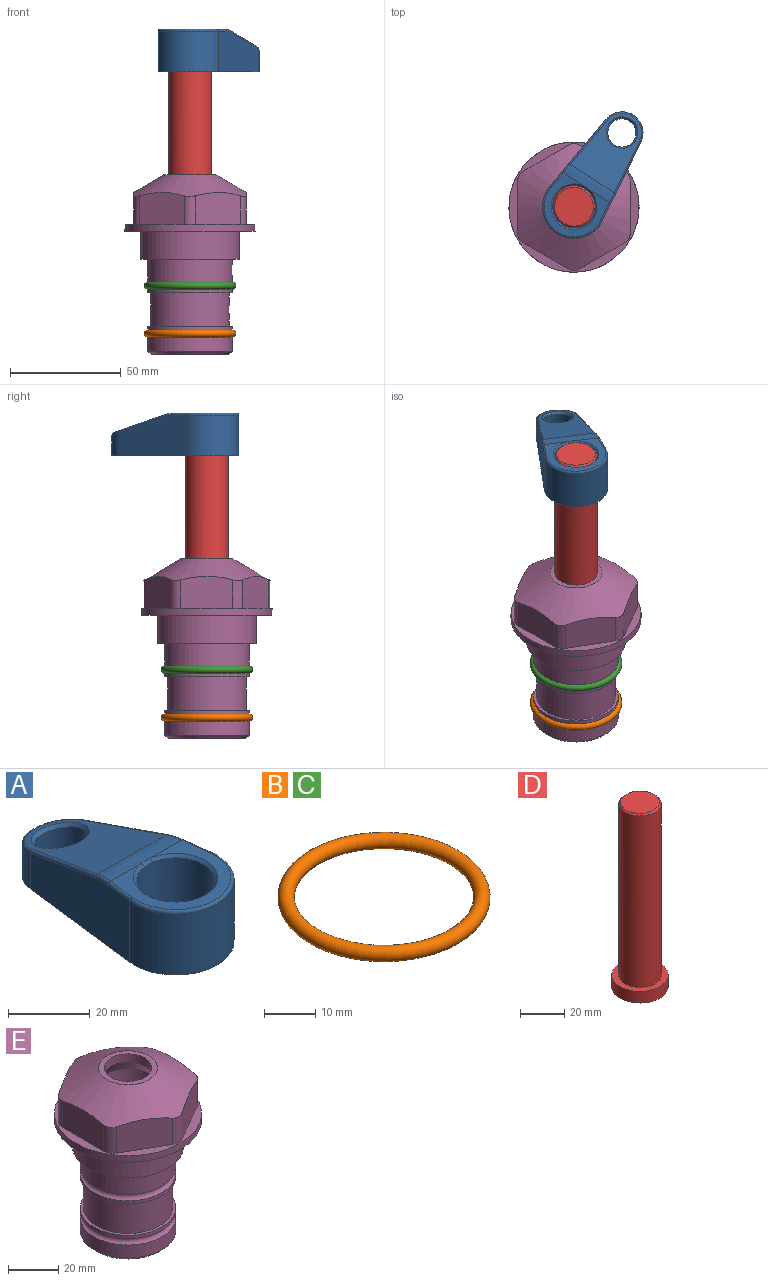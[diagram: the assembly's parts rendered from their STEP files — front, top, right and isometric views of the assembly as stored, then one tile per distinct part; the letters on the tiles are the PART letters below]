
ASSEMBLY  parts=5 mates=4
PART A: 31 faces, bbox 31.7x65.5x19.8 mm
  f0: plane 39.12x18.26mm, normal (0.99,0.12,0), area 612.2mm2, adj f1,f4,f7,f11,f13,f15
  f1: cylinder r=9.53mm len=18.91mm, axis (0,0,-1), area 296.1mm2, adj f0,f2,f7,f17
  f2: plane 39.12x18.26mm, normal (-0.99,0.12,0), area 612.2mm2, adj f1,f4,f7,f12,f14,f16
  f3: cylinder r=6.35mm len=12.7mm, axis (0,0,-1), area 362.4mm2, adj f7,f18
  f4: cylinder r=14.29mm len=28.58mm, axis (0,0,-1), area 882.2mm2, adj f0,f2,f7,f10
  f5: cylinder r=9.53mm len=19.05mm, axis (0,0,-1), area 1092.6mm2, adj f7,f19,f20
  f6: plane 26.99x23.69mm, normal (0,0,1), area 216.2mm2, adj f9,f10,f11,f12,f19
  f7: plane 63.5x28.58mm, normal (0,0,-1), area 661.8mm2, adj f0,f1,f2,f3,f4,f5,f22,f23
  f8: plane 33.52x23.6mm, normal (0,0.26,0.97), area 486mm2, adj f9,f15,f16,f17,f18
  f9: cylinder r=19.05mm len=24.72mm, axis (1,0,0), area 120.4mm2, adj f6,f8,f13,f14,f20
  f10: torus R=13.49mm, axis (0,0,1), area 59mm2, adj f4,f6,f11,f12
  f11: cylinder r=0.79mm len=8.67mm, axis (0.12,-0.99,0), area 10.8mm2, adj f0,f6,f10,f13
  f12: cylinder r=0.79mm len=8.67mm, axis (0.12,0.99,0), area 10.8mm2, adj f2,f6,f10,f14
  f13: bspline ~4.95x1.42mm, area 6.1mm2, adj f0,f9,f11,f15
  f14: bspline ~4.95x1.42mm, area 6.1mm2, adj f2,f9,f12,f16
  f15: cylinder r=0.79mm len=25.95mm, axis (0.12,-0.96,0.26), area 32.9mm2, adj f0,f8,f13,f17
  f16: cylinder r=0.79mm len=25.95mm, axis (0.12,0.96,-0.26), area 32.9mm2, adj f2,f8,f14,f17
  f17: bspline ~18.91x8.38mm, area 30mm2, adj f1,f8,f15,f16
  f18: bspline ~14.29x14.29mm, area 48.3mm2, adj f3,f8
  f19: cone r=9.53mm half-angle=45deg, axis (0,0,1), area 66.5mm2, adj f5,f6,f20
  f20: bspline ~3.22x0.96mm, area 3.5mm2, adj f5,f9,f19
  f21: plane 2.75x2.72mm, normal (0,0,-1), area 2.9mm2, adj f23,f25,f28
  f22: plane 23.05x15.88mm, normal (-0.99,-0.12,0), area 323.6mm2, adj f7,f25,f26,f27,f28,f29
  f23: plane 23.05x15.88mm, normal (0.99,-0.12,0), area 323.6mm2, adj f7,f21,f25,f27,f28,f30
  f24: cylinder r=9.53mm len=10.69mm, axis (0,0,-1), area 114.7mm2, adj f7,f27,f29,f30
  f25: cylinder r=12.7mm len=20.59mm, axis (0,0,-1), area 381.1mm2, adj f7,f21,f22,f23,f26,f28
  f26: plane 2.75x2.72mm, normal (0,0,-1), area 2.9mm2, adj f22,f25,f28
  f27: plane 19.72x18.37mm, normal (0,-0.26,-0.97), area 291.8mm2, adj f22,f23,f24,f28,f29,f30
  f28: cylinder r=15.88mm len=19.92mm, axis (1,0,0), area 54.8mm2, adj f21,f22,f23,f25,f26,f27
  f29: cylinder r=1.59mm len=11mm, axis (0,0,-1), area 34.7mm2, adj f7,f22,f24,f27
  f30: cylinder r=1.59mm len=11mm, axis (0,0,-1), area 34.7mm2, adj f7,f23,f24,f27
PART B: 1 faces, bbox 44.7x44.7x3.2 mm
  f0: torus R=19.05mm, axis (0,0,1), area 1193.9mm2
PART C: same geometry as B
PART D: 6 faces, bbox 25.4x25.4x101.6 mm
  f0: plane 17.46x17.46mm, normal (0,0,1), area 239.5mm2, adj f5
  f1: plane 25.4x25.4mm, normal (0,0,-1), area 506.7mm2, adj f2
  f2: cylinder r=12.7mm len=25.4mm, axis (0,0,1), area 506.7mm2, adj f1,f3
  f3: plane 25.4x25.4mm, normal (0,0,1), area 221.7mm2, adj f2,f4
  f4: cylinder r=9.53mm len=94.46mm, axis (0,0,1), area 5653mm2, adj f3,f5
  f5: cone r=8.73mm half-angle=45deg, axis (0,0,-1), area 64.4mm2, adj f0,f4
PART E: 36 faces, bbox 58.7x58.7x81 mm
  f0: cylinder r=17.78mm len=35.56mm, axis (0,0,1), area 1670.8mm2, adj f23,f24,f31
  f1: cylinder r=19.05mm len=38.1mm, axis (0,0,1), area 1191.9mm2, adj f26,f27,f30
  f2: plane 58.66x58.66mm, normal (0,0,-1), area 1150.6mm2, adj f3,f28
  f3: cylinder r=29.33mm len=58.66mm, axis (0,0,-1), area 585.1mm2, adj f2,f4
  f4: plane 58.66x58.66mm, normal (0,0,1), area 475.9mm2, adj f3,f5,f6,f7,f8,f9,f10,f11
  f5: plane 20.32x14.34mm, normal (-0.5,0.87,0), area 324.4mm2, adj f4,f15,f16,f17
  f6: plane 20.32x14.34mm, normal (0.5,0.87,0), area 324.4mm2, adj f4,f14,f15,f17
  f7: plane 23.48x14.34mm, normal (1,0,0), area 324.4mm2, adj f4,f13,f14,f17
  f8: plane 20.32x14.34mm, normal (0.5,-0.87,0), area 324.4mm2, adj f4,f12,f13,f17
  f9: plane 20.32x14.34mm, normal (-0.5,-0.87,0), area 324.4mm2, adj f4,f11,f12,f17
  f10: plane 23.48x14.34mm, normal (-1,0,0), area 324.4mm2, adj f4,f11,f16,f17
  f11: cylinder r=5.08mm len=12.85mm, axis (0,0,-1), area 67.2mm2, adj f4,f9,f10,f17
  f12: cylinder r=5.08mm len=12.85mm, axis (0,0,-1), area 67.2mm2, adj f4,f8,f9,f17
  f13: cylinder r=5.08mm len=12.85mm, axis (0,0,-1), area 67.2mm2, adj f4,f7,f8,f17
  f14: cylinder r=5.08mm len=12.85mm, axis (0,0,-1), area 67.2mm2, adj f4,f6,f7,f17
  f15: cylinder r=5.08mm len=12.85mm, axis (0,0,-1), area 67.2mm2, adj f4,f5,f6,f17
  f16: cylinder r=5.08mm len=12.85mm, axis (0,0,-1), area 67.2mm2, adj f4,f5,f10,f17
  f17: cone r=11.73mm half-angle=60deg, axis (0,0,-1), area 2071.8mm2, adj f5,f6,f7,f8,f9,f10,f11,f12
  f18: plane 23.46x23.46mm, normal (0,0,1), area 147.4mm2, adj f17,f35
  f19: plane 34.93x34.93mm, normal (0,0,-1), area 958mm2, adj f29
  f20: cylinder r=19.05mm len=38.1mm, axis (0,0,1), area 760.1mm2, adj f21,f29
  f21: torus R=19.05mm, axis (0,0,1), area 565.3mm2, adj f20,f22
  f22: cylinder r=19.05mm len=38.1mm, axis (0,0,1), area 190mm2, adj f21,f23
  f23: plane 38.1x38.1mm, normal (0,0,1), area 146.9mm2, adj f0,f22
  f24: plane 38.1x38.1mm, normal (0,0,-1), area 146.9mm2, adj f0,f25
  f25: cylinder r=19.05mm len=38.1mm, axis (0,0,1), area 190mm2, adj f24,f26
  f26: torus R=19.05mm, axis (0,0,1), area 565.3mm2, adj f1,f25
  f27: plane 44.45x44.45mm, normal (0,0,-1), area 411.7mm2, adj f1,f28
  f28: cylinder r=22.23mm len=44.45mm, axis (0,0,1), area 1773.5mm2, adj f2,f27
  f29: cone r=19.05mm half-angle=45deg, axis (0,0,1), area 257.5mm2, adj f19,f20
  f30: cylinder r=3.17mm len=6.75mm, axis (-1,0,0), area 128mm2, adj f1,f33
  f31: cylinder r=3.17mm len=6.35mm, axis (-1,0,0), area 102.5mm2, adj f0,f33
  f32: plane 25.4x25.4mm, normal (0,0,1), area 506.7mm2, adj f33
  f33: cylinder r=12.7mm len=66.42mm, axis (0,0,-1), area 5236.2mm2, adj f30,f31,f32,f34
  f34: cone r=9.53mm half-angle=30deg, axis (0,0,-1), area 443.4mm2, adj f33,f35
  f35: cylinder r=9.53mm len=19.05mm, axis (0,0,-1), area 240.9mm2, adj f18,f34
PLACE A rot(axis=(0,0,-1),33deg) t=(0,0,27.55)mm
PLACE B t=(0,0,-21.59)mm
PLACE C at identity
PLACE D rot(axis=(0,0,-1),33deg) t=(0,0,27.55)mm
PLACE E at identity fixed
MATE cylindrical E.f0 <-> D.f2  axis (0,0,1) through (0,0,-50.55)mm
MATE fastened C.f0 <-> E.f0  axis (0,0,1) through (0,0,-24.51)mm
MATE fastened D.f2 <-> A.f4  axis (0,0,1) through (0,0,91.05)mm
MATE fastened B.f0 <-> E.f0  axis (0,0,1) through (0,0,-46.1)mm
